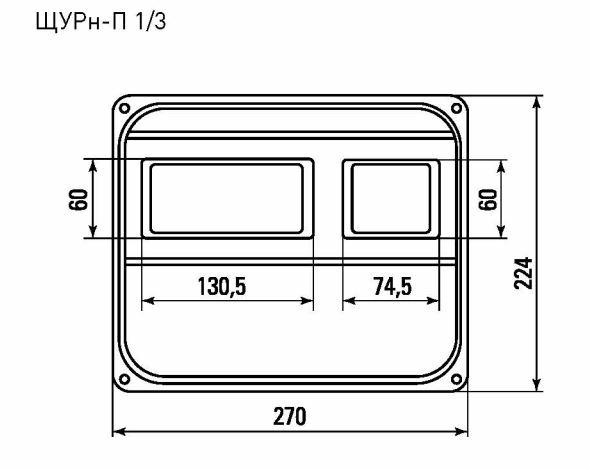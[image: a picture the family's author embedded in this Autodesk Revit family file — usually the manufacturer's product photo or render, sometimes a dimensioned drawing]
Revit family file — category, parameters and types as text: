
# Revit family: EKF_EE_ЯУР_Basic
name_source: partatom
category: Электрооборудование
units: mm (PartAtom-declared; Revit-internal decimal feet)

## family parameters
Всегда вертикально = Да
На основе рабочей плоскости = Нет
Общий = Нет
При загрузке вырезать с полостями = Нет
Размер круглого соединителя = Использовать диаметр
Тип детали = Силовой щит
Точка расчета площади = Да

## types (4) — shared parameters
ADSK_Единица измерения = компл.
ADSK_Завод-изготовитель = EKF
ADSK_Классификация нагрузок = Прочее
ADSK_Количество = 1
ADSK_Количество фаз = 3
ADSK_Коэффициент мощности = 1
ADSK_Материал = RAL 7035_Сталь
ADSK_Напряжение = 400 В
ADSK_Номинальная мощность = 0 Вт
ADSK_Полная мощность = 0 В·А
ADSK_Размер_Глубина = 150 мм
ADSK_Размер_Ширина = 300 мм
ADSK_Ток = 125 А
Изготовитель = EKF
Количество модулей на DIN-рейке = 12
Максимальное количество модулей = 12
Серия номенклатуры = Basic
Степень защиты IP = IP31
ТВ = EKF
Тип установки = Навесной
zero-valued in all types: ADSK_Масса

## per-type parameters (varying)
| type | ADSK_Код изделия | ADSK_Марка | ADSK_Наименование | ADSK_Обозначение | ADSK_Размер_Высота | Количество DIN-реек | Описание | Тип |
| ЯУР на 2 счетчика с двумя DIN-рейками (600х300х150) EKF Basic | uerm-din-600-2 | ЯУР на 2 счетчика с двумя DIN-рейками | ЯУР на 2 счетчика с двумя DIN-рейками (600х300х150) EKF BasicЯУР на 2 счетчика с двумя DIN-рейками (600х300х150) EKF Basic | ЯУР на 2 счетчика с двумя DIN-рейками | 600 мм | 2 | ЯУР на 2 счетчика с двумя DIN-рейками (600х300х150) EKF BasicЯУР на 2 счетчика с двумя DIN-рейками (600х300х150) EKF Basic | 206 мм |
| ЯУР с двумя DIN-рейками (400х300х150) EKF Basic | uerm-din-400 | ЯУР с двумя DIN-рейками (400х300х150) | ЯУР с двумя DIN-рейками (400х300х150) EKF BasicЯУР с двумя DIN-рейками (400х300х150) EKF Basic | ЯУР с двумя DIN-рейками (400х300х150) | 400 мм | 2 | ЯУР с двумя DIN-рейками (400х300х150) EKF BasicЯУР с двумя DIN-рейками (400х300х150) EKF Basic | 207 мм |
| ЯУР с монтажной панелью и двумя DIN-рейками (600х300х150) EKF Basic | uerm-mp-600 | ЯУР с монтажной панелью и двумя DIN-рейками | ЯУР с монтажной панелью и двумя DIN-рейками (600х300х150) EKF BasicЯУР с монтажной панелью и двумя DIN-рейками (600х300х150) EKF Basic | ЯУР с монтажной панелью и двумя DIN-рейками | 600 мм | 2 | ЯУР с монтажной панелью и двумя DIN-рейками (600х300х150) EKF BasicЯУР с монтажной панелью и двумя DIN-рейками (600х300х150) EKF Basic | 208 мм |
| ЯУР с одной DIN-рейкой (300х300х150) EKF Basic | uerm-din-300 | ЯУР с одной DIN-рейкой | ЯУР с одной DIN-рейкой (300х300х150) EKF BasicЯУР с одной DIN-рейкой (300х300х150) EKF Basic | ЯУР с одной DIN-рейкой | 300 мм | 1 | ЯУР с одной DIN-рейкой (300х300х150) EKF BasicЯУР с одной DIN-рейкой (300х300х150) EKF Basic | 209 мм |
